# Revit family: LU-75_GENERADO
name_source: partatom
category: Equipos especializados
revit_build: Autodesk Revit 2014 (Build: 20131024_2115(x64)
units: mm (PartAtom-declared; Revit-internal decimal feet)

## types (5) — shared parameters
Cold Water Consumption = 6
Cold Water Maximum Pressure = 0.4 Pa
Cold Water Minimum Pressure = 0.2 Pa
Direct Waste Connection Height = 1850 mm  [stored 6.06955 ft]
Fabricante = SAMMIC S.L.
Foodservice Equipment Identifier = Sí
HP = 17.3
Revision Code = 1
Specification by Manufacturer = Max. loading height: 650mm.
URL = https://www.sammic.com
URL Cutsheet = http://www.sammic.com
Watts = 12900 W
Weight in Pounds = 432.1
Width = 922 mm  [stored 3.02493 ft]

## per-type parameters (varying)
| type | Comentarios de tipo | Cycle | FL Amps | Modelo | Phase | Volts |
| Utensil washer LU-75 230-400/50/3N | 780 x 700 mm. basket

ELECTRICAL DATA:

230V/50Hz/3~ (34.2A) | 50 Hz | 20 A | 1300580 | 3 | 400 V |
| Utensil washer LU-75B 230-400/50/3N (with drain pump) | 780 x 700 mm. basket

ELECTRICAL DATA:

230V/50Hz/3~ (34.2A) | 50 Hz | 20 A | 1300584 | 3 | 400 V |
| Utensil washer LU-75 440/60/3 without N | 780 x 700 mm. basket | 0 Hz | 0 A | 1300583 | 0 | 0 V |
| Utensil washer LU-75 220/60/3 | 780 x 700 mm. basket | 0 Hz | 0 A | 1300582 | 0 | 0 V |
| Utensil washer LU-75 400/50/3 without N | 780 x 700 mm. basket | 0 Hz | 0 A | 1300581 | 0 | 0 V |

note: column(s) folded — value = type name in every type: Descripción

note: [stored X ft] marks values corroborated as IEEE doubles in the binary element streams (Revit-internal decimal feet)
